# Revit family: ASSA_ABLOY_TS100
name_source: partatom
category: Generic Models
units: mm (PartAtom-declared; Revit-internal decimal feet)

## family parameters
Always vertical = Yes
Can host rebar = No
Cut with Voids When Loaded = No
Part Type = Normal
Room Calculation Point = No
Round Connector Dimension = Use Diameter
Shared = No
Work Plane-Based = No

## types (1)
- TS100
    Access control/Biometrics = Yes
    AccessoryOptions = Contact manufacturer
    Anti-tailgating/Anti-piggybacking = No
    AntiFingerTrapRequirement = No
    BreakoutFacility = No
    Burglar resistance = No
    Colour = Customer specific
    Construction Type = Tripod turnstile
    Default Elevation = 0 mm  [stored 0 ft]
    Description = Tripod Turnstile
    DoorIncluded = Yes
    DoorsetFasteners = Screws
    DoorsetOperation = Automatic
    DoorsetOptions = no
    DrumWallOptions = Metal
    ElectronicLock = Yes
    FireExit = Yes
    FrameFinishOptions = Powder coated, Anodized, Clad in stainless steel, etc.
    FrameProfile = Aluminium
    FrameSeal = Yes
    GlassLayers = 0
    GlassThickness1 = 0 mm  [stored 0 ft]
    GlassThickness2 = 0 mm  [stored 0 ft]
    HandicapAccessible = No
    HasDrive = Yes
    IsExternal = Yes
    LeafColourOptions = All RAL, customer specific
    Manufacturer = Tansa
    ManufacturerURL = https://www.assaabloyentrance.com
    Material = Aluminum
    Model = TS
    ModelReference = Depends on the configuration
    NominalHeight = 1006 mm  [stored 3.30052 ft]
    NominalLength = 1200 mm
    NominalWidth = 758 mm  [stored 2.48688 ft]
    OperatingTemperature = -10º to +70ºC
    PassageWidthOptions = 530
    ReplacementCost = Depends on the configuration and door type
    SafetyDevices = Force Limitations and Safety Sensors
    SelfClosing = Yes
    ServiceLifeDuration = 10-15 years
    Shape = Rectangular shaped
    ThresholdRequired = No
    URL = https://www.assaabloyentrance.com
    WarrantyDescription = Depends on country
    Weight = Depends on configuration and size

note: [stored X ft] marks values corroborated as IEEE doubles in the binary element streams (Revit-internal decimal feet)

## geometry (parser evidence)
native form markers: Blend x4, Sweep x9
no freeform markers — native parametric forms only
